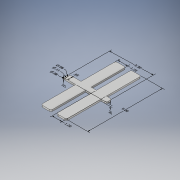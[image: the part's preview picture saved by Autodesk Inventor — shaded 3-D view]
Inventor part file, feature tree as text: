
AUTODESK INVENTOR PART (.ipt)
format: ipt  version: 2018 (Build 220112000, 112)  size: 193,024 bytes
history: native  units: in
note: dims shown in document units (in); Inventor stores cm internally (conversion verified against a paired STEP export)
features: other x11, extrude x3, sketch x3, fillet x2
ambient origin geometry x8: Origin, YZ Plane, XZ Plane, XY Plane, X Axis, Y Axis, Z Axis, Center Point
bodies: Solid1 (feature_tree)
feature tree (19):
  other  "Annotations"
  extrude  "Extrusion1"  Depth=0.65in
  fillet  "Fillet1"  Radius=0.65in
  fillet  "Fillet2"  Radius=1.2in
  extrude  "Extrusion2"  Depth=1.2in
  extrude  "Extrusion3"  Depth=1.2in
  sketch  "Sketch1"  dims[d0=5.3in d1=0.65in d2=0.65in d3=1.2in]
  sketch  "Sketch2"  dims[d4=0.65in d5=1.2in]
  sketch  "Sketch3"  dims[d7=4.5in d8=1.2in d9=4.5in d10=1.2in d11=4.5in d12=1.2in d13=4.5in d14=1.2in d15=0.2in d16=0.0in d17=0.2in d18=0.2in d19=0.32in d20=0.15in d21=0.0in d22=0.15in d23=0.11in d24=0.15in d25=0.15in d26=0.08in d27=0.08in d28=0.05in d29=0.0in d30=0.2114in d31=0.08in d32=2.3414in d33=0.11in d34=2.1812in d35=0.08in d36=0.0497in d37=0.1242in d38=0.05in d39=0.1889in d40=0.23in d41=0.65in d42=0.2453in d43=0.2011in d44=0.2in d45=0.1552in d46=0.0902in d47=5.3021in d48=0.0535in d49=0.3221in d50=1.2in d51=0.1045in d52=0.2674in d53=1.2in d54=0.1834in d55=0.2431in d56=9.0in]
  other  "Diameter Dimension 1"
  other  "Diameter Dimension 2"
  other  "Diameter Dimension 3"
  other  "Linear Dimension 1"
  other  "Linear Dimension 2"
  other  "Linear Dimension 3"
  other  "Linear Dimension 4"
  other  "Linear Dimension 5"
  other  "Linear Dimension 6"
  other  "Linear Dimension 7"
